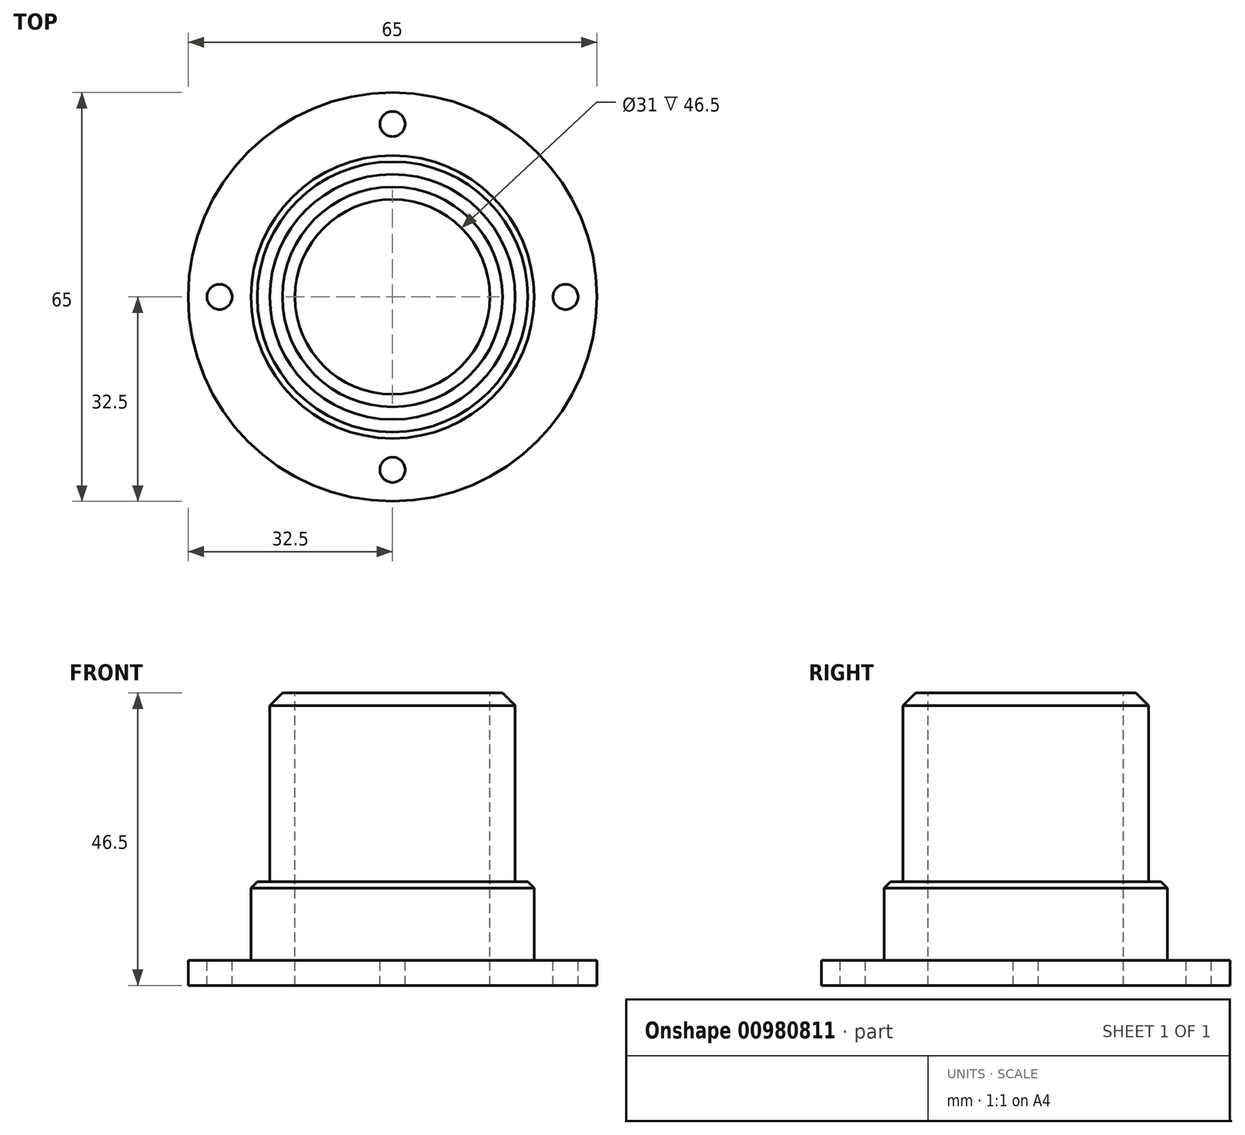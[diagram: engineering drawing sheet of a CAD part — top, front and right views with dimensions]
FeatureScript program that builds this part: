
annotation { "Feature Type Name" : "Feature", "Feature Type Description" : "" }
export const myFeature = defineFeature(function(context is Context, id is Id, definition is map)
    precondition{}
    {
        {
            var Q0;
            Q0=qCreatedBy(makeId("Top.planeOp"),FACE);
            var sketch = newSketch(context, id + "F0", { "sketchPlane" : qUnion([Q0])});
            skCircle(sketch, "E0", {"center": v(0, 0) * mm, "radius": 32.5 * mm});
            skSolve(sketch);
        }
        {
            var Q0;
            Q0 = qSketchRegion(id + "F0", true);
            extrude(context, id + "F1", {"entities" : qUnion([Q0]), "depth" : 4 * mm, "offsetDistance" : 25 * mm});
        }
        {
            var Q0;
            Q0=makeQuery(id+"F1.opExtrude","CAP_FACE",FACE,{"disambiguationData":[OSD([sQuery(id+"F0.wireOp",EDGE,"E0")])],"isStart":false});
            var sketch = newSketch(context, id + "F2", { "sketchPlane" : qUnion([Q0])});
            skCircle(sketch, "E1", {"center": v(0, 0) * mm, "radius": 22.5 * mm});
            skSolve(sketch);
        }
        {
            var Q0;
            Q0 = qSketchRegion(id + "F2", true);
            extrude(context, id + "F3", {"entities" : qUnion([Q0]), "operationType" : NewBodyOperationType.ADD, "depth" : 12.5 * mm, "offsetDistance" : 25 * mm});
        }
        {
            var Q0;
            Q0=makeQuery(id+"F3.opExtrude","CAP_FACE",FACE,{"disambiguationData":[OSD([sQuery(id+"F2.wireOp",EDGE,"E1")])],"isStart":false});
            var sketch = newSketch(context, id + "F4", { "sketchPlane" : qUnion([Q0])});
            skCircle(sketch, "E2", {"center": v(0, 0) * mm, "radius": 19.5 * mm});
            skSolve(sketch);
        }
        {
            var Q0;
            Q0 = qSketchRegion(id + "F4", true);
            extrude(context, id + "F5", {"entities" : qUnion([Q0]), "operationType" : NewBodyOperationType.ADD, "depth" : 30 * mm, "offsetDistance" : 25 * mm});
        }
        {
            var Q0;
            Q0=makeQuery(id+"F5.opExtrude","CAP_FACE",FACE,{"disambiguationData":[OSD([sQuery(id+"F4.wireOp",EDGE,"E2")])],"isStart":false});
            var sketch = newSketch(context, id + "F6", { "sketchPlane" : qUnion([Q0])});
            skCircle(sketch, "E3", {"center": v(0, 0) * mm, "radius": 15.5 * mm});
            skSolve(sketch);
        }
        {
            var Q0;
            Q0 = qSketchRegion(id + "F6", true);
            extrude(context, id + "F7", {"entities" : qUnion([Q0]), "operationType" : NewBodyOperationType.REMOVE, "endBound" : BoundingType.THROUGH_ALL, "oppositeDirection" : true, "depth" : 25 * mm, "offsetDistance" : 25 * mm});
        }
        {
            var Q0;
            Q0=makeQuery(id+"F1.opExtrude","CAP_FACE",FACE,{"disambiguationData":[OSD([sQuery(id+"F0.wireOp",EDGE,"E0")])],"isStart":false});
            var sketch = newSketch(context, id + "F8", { "sketchPlane" : qUnion([Q0])});
            skLineSegment(sketch, "E4", {"start": v(0, 39.84) * mm, "end": v(0, -38.09) * mm, "construction": true});
            skLineSegment(sketch, "E5", {"start": v(-48.97, 0) * mm, "end": v(51.42, 0) * mm, "construction": true});
            skCircle(sketch, "E6", {"center": v(0, 0) * mm, "radius": 27.5 * mm, "construction": true});
            skCircle(sketch, "E7", {"center": v(0, 27.5) * mm, "radius": 2 * mm});
            skCircle(sketch, "E8", {"center": v(27.5, 0) * mm, "radius": 2 * mm});
            skCircle(sketch, "E9", {"center": v(0, -27.5) * mm, "radius": 2 * mm});
            skCircle(sketch, "E10", {"center": v(-27.5, 0) * mm, "radius": 2 * mm});
            skSolve(sketch);
        }
        {
            var Q0;
            Q0 = qSketchRegion(id + "F8", true);
            extrude(context, id + "F9", {"entities" : qUnion([Q0]), "operationType" : NewBodyOperationType.REMOVE, "endBound" : BoundingType.THROUGH_ALL, "oppositeDirection" : true, "depth" : 25 * mm, "offsetDistance" : 25 * mm});
        }
        {
            var Q0;
            Q0=makeQuery(id+"F5.opExtrude","CAP_EDGE",EDGE,{"disambiguationData":[OSD([sQuery(id+"F4.wireOp",EDGE,"E2")])],"isStart":false});
            chamfer(context, id + "F10", {"entities" : qUnion([Q0]), "width" : 2 * mm, "tangentPropagation" : true});
        }
        {
            var Q0;
            Q0=makeQuery(id+"F3.opExtrude","CAP_EDGE",EDGE,{"disambiguationData":[OSD([sQuery(id+"F2.wireOp",EDGE,"E1")])],"isStart":false});
            chamfer(context, id + "F11", {"entities" : qUnion([Q0]), "width" : 1 * mm, "tangentPropagation" : true});
        }
    });
